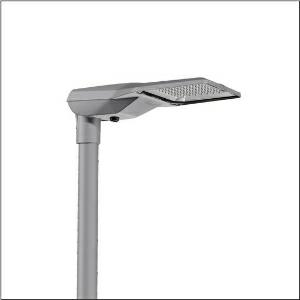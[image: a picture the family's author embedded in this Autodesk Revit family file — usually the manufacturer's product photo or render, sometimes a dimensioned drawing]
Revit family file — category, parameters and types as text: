
# Revit family: streetlight_sl_21_iq_midi___p0_8ab_5xe3r31u08nb_f32c
name_source: partatom
category: Lighting Fixtures
units: mm (PartAtom-declared; Revit-internal decimal feet)

## family parameters
Cut with Voids When Loaded = No
Host = Face
Light Source = No
Part Type = Normal
Room Calculation Point = No
Round Connector Dimension = Use Diameter
Shared = No

## types (1)
- --- (1 x LED, 18710 lm, 136.6 W, 3000K)
    Apparent Load = 137 VA
    CIE Flux Codes = 39 72 97 100 100
    Color Rendering = 70
    Color Temperature = 3000K
    Default Elevation = 1800 mm
    Description = Streetlight SL 21 iQ midi, mast luminaire, primary light control with lens, of PMMA, primary optical cover: cover, of toughened safety glass, transparent, light distribution: P0.8aB, light emission: direct distribution, primary light characteristic: asymmetric, installation type: post-top, side-entry, LED, High Power LED, rated luminous flux: 18.710lm, luminous efficacy: 137lm/W, light colour: 730, colour temperature: 3000K, control gear: iQ-Street Remote, D4i with power reduction, control: pre-setting: logarithmic dimming characteristic, Street-Remote, Auto-Match, Temp-Guard, Lumen-Switch, Night-Set, Smart-Wire, Light-Fading, Desk-Remote (wireless, voltage-free reading and setting of iQ features in the workshop via application-optimized NFC function/RFID function), optimised constant luminous flux control (CLO 2.0), mains connection: 230..240V, AC, 50/60Hz, start of lifetime: 137W, end of service life: 144W, reduction: 61W, luminaire housing, of diecast aluminium, powder-coated, SITECO metallic grey (DB 702S), corrosivity category C5 high according to DIN EN ISO 12944, please order mast flange separately, inclination adjustable: 0°, 5°, 10°, 15°, sealing non-destructively replaceable, multi-level sealing system, length: 644mm, width: 335mm, height: 110mm, mast flange for spigot size: 42mm (side-entry): 5XC10008XM4, 60/48mm (side-entry/post-top): 5XC10108XM2, 76/60mm (side-entry/post-top): 5XC10108XM1, mounting height: 4..8m, Smart Interface below, protection rating (complete): IP66, insulation class (complete): insulation class II (safety insulation), certification: CE, ENEC, ENEC+, VDE, impact resistance: IK10, permissible operating ambient temperature for outdoor applications: -40..+50°C, standard-compliant lighting for roads and squares, packaging unit: 1 piece

Light Distribution: P0.8aB
    Height = 111 mm
    Lamp = 1 x LED
    Lamp Light Flux = 18710 lm
    Lamp Power = 136.6 W
    Lamp count = 1
    Length = 644 mm
    Luminous efficacy = 137 lm/W
    Manufacturer = Siteco
    ModVariant = No
    Model = 5XE3R31U08NB
    Number of Poles = 1
    OnlyDefault = Yes
    Power Factor = 1
    Product Name = Streetlight SL 21 iQ midi | P0.8aB
    Product group = mast luminaire | pylon top
    ProductGroupID = 6100
    Protection Class = Protection class II
    Protection Degree = IP 66
    RLX_Detail_Level = 1
    RLX_Emergency_Light_Flux = 0 lm
    RLX_Emergency_Type = 0
    RLX_Emergency_Type_DB = No
    RlxData = <blob elided: 90301 chars, md5=f90e8a30>
    Socket = socket
    Standby Power = 0 W
    System Light Flux = 18710 lm
    System Power = 137 W
    Type Comments = factory setting: luminous flux: 100 % | dim-lin: 254 | 733 mA
    Type Image = l_1004300.jpg
    URL = http://relux.com
    VarID = @adj_078991
    Voltage = 0 V
    Weight = 0.00 kg
    Width = 336 mm

## geometry (parser evidence)
native form markers: Blend x4, Sweep x12
no freeform markers — native parametric forms only
